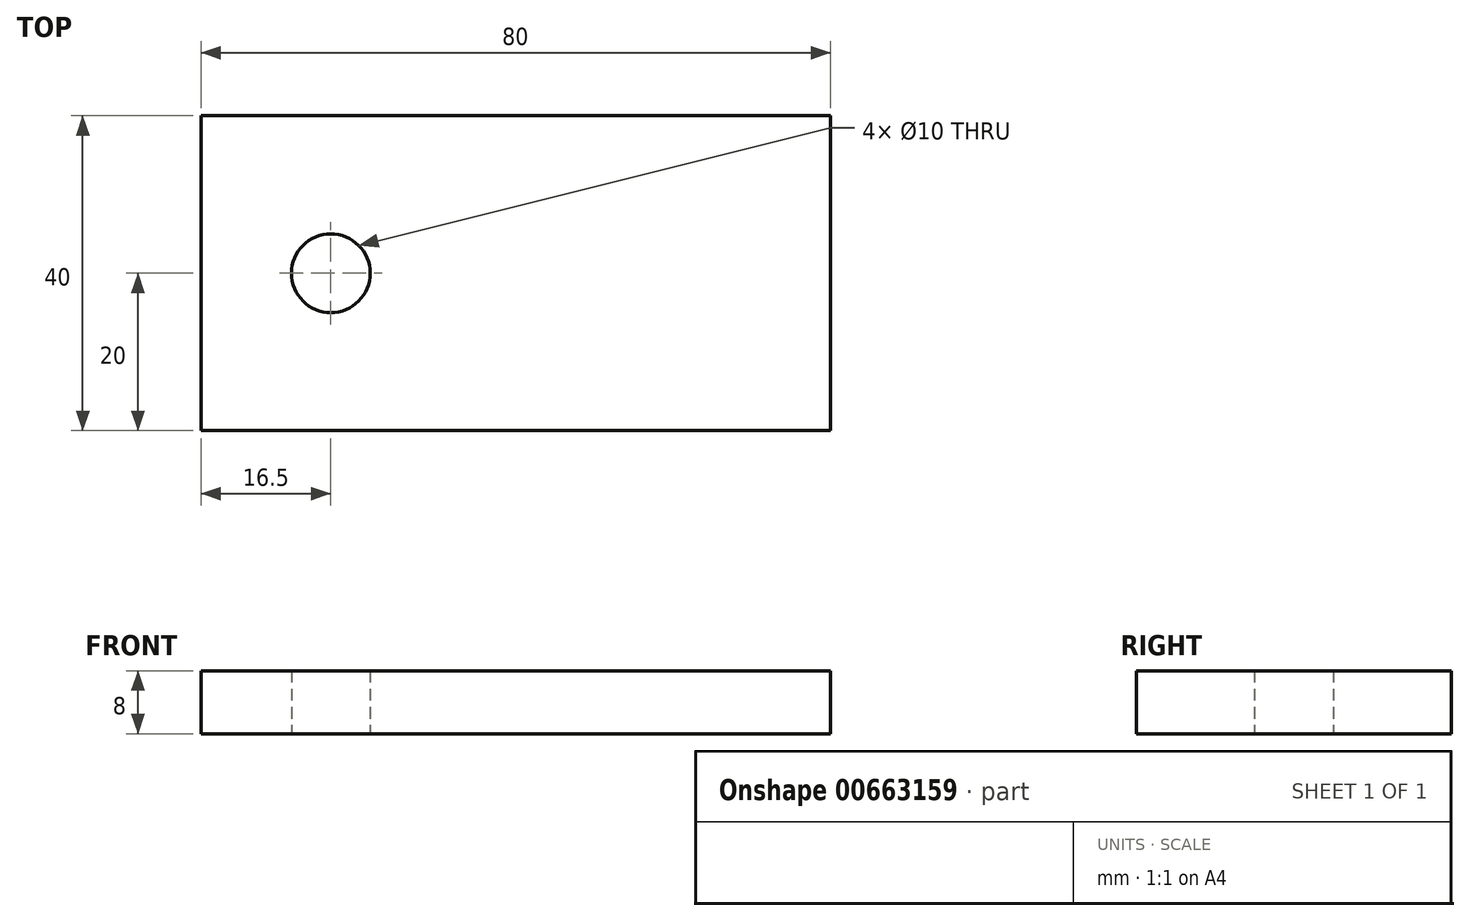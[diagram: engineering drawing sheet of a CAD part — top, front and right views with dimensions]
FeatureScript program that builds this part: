
annotation { "Feature Type Name" : "Feature", "Feature Type Description" : "" }
export const myFeature = defineFeature(function(context is Context, id is Id, definition is map)
    precondition{}
    {
        {
            var Q0;
            Q0=qCreatedBy(makeId("Top.planeOp"),FACE);
            var sketch = newSketch(context, id + "F0", { "sketchPlane" : qUnion([Q0])});
            skLineSegment(sketch, "E0.bottom", {"start": v(40, 20) * mm, "end": v(-40, 20) * mm});
            skLineSegment(sketch, "E0.top", {"start": v(40, -20) * mm, "end": v(-40, -20) * mm});
            skLineSegment(sketch, "E0.left", {"start": v(40, 20) * mm, "end": v(40, -20) * mm});
            skLineSegment(sketch, "E0.right", {"start": v(-40, 20) * mm, "end": v(-40, -20) * mm});
            skPoint(sketch, "E0.middle", {"position": v(0, 0) * mm});
            skCircle(sketch, "E1", {"center": v(-23.5, 0) * mm, "radius": 5 * mm});
            skSolve(sketch);
        }
        {
            var Q0;
            Q0=makeQuery(id+"F0.imprint","IMPRINT",FACE,{"disambiguationData":[TD([[makeQuery(id+"F0.imprint","IMPRINT",EDGE,{"derivedFrom":sQuery(id+"F0.wireOp",EDGE,"E0.bottom")}),1.0]])]});
            extrude(context, id + "F1", {"entities" : qUnion([Q0]), "endBound" : BoundingType.SYMMETRIC, "depth" : 8 * mm, "offsetDistance" : 25 * mm});
        }
    });
